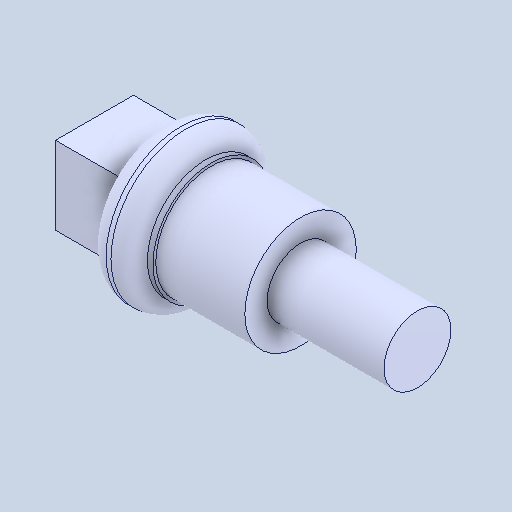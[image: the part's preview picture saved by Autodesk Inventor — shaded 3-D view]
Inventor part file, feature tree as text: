
AUTODESK INVENTOR PART (.ipt)
format: ipt  version: 2024.1 (Build 281209000, 209)  size: 144,384 bytes
history: native  units: in
note: dims shown in document units (in); Inventor stores cm internally (conversion verified against a paired STEP export)
features: fillet x1
ambient origin geometry x8: Origin, YZ Plane, XZ Plane, XY Plane, X Axis, Y Axis, Z Axis, Center Point
bodies: Solid1 (feature_tree)
feature tree (1):
  fillet  "Fillet1"  [1 undecoded]
note: 1 required parameter value undecoded (feature->parameter linkage not recoverable at this tier; creation-order binding heuristic only, values carry confidence <= 0.55)
